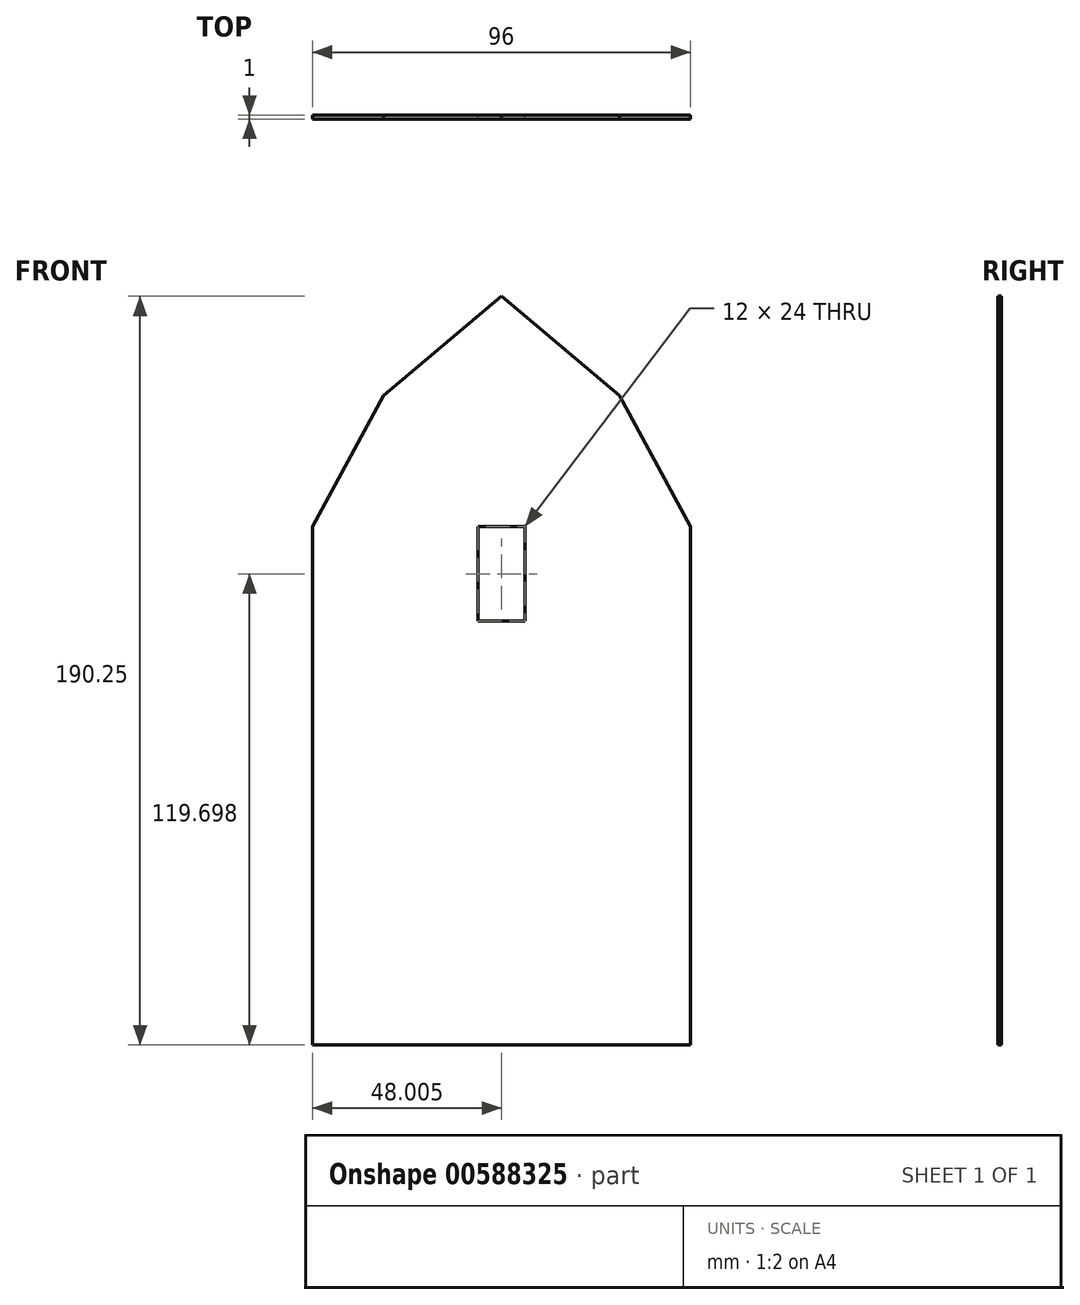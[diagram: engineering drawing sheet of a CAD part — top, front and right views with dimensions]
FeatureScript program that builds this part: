
annotation { "Feature Type Name" : "Feature", "Feature Type Description" : "" }
export const myFeature = defineFeature(function(context is Context, id is Id, definition is map)
    precondition{}
    {
        {
            var Q0;
            Q0=qCreatedBy(makeId("Front.planeOp"),FACE);
            var sketch = newSketch(context, id + "F0", { "sketchPlane" : qUnion([Q0])});
            skLineSegment(sketch, "E0", {"start": v(118.21, 7.75) * mm, "end": v(118.21, 40.5) * mm});
            skLineSegment(sketch, "E1", {"start": v(118.21, 40.5) * mm, "end": v(118.21, 113.5) * mm});
            skLineSegment(sketch, "E2", {"start": v(118.21, 113.5) * mm, "end": v(118.21, 116.7) * mm});
            skLineSegment(sketch, "E3", {"start": v(76.21, 116.7) * mm, "end": v(64.21, 116.7) * mm});
            skLineSegment(sketch, "E4", {"start": v(118.21, 7.75) * mm, "end": v(70.21, 7.75) * mm});
            skLineSegment(sketch, "E5", {"start": v(22.21, 7.75) * mm, "end": v(22.21, 116.7) * mm});
            skLineSegment(sketch, "E6", {"start": v(70.21, 116.7) * mm, "end": v(76.21, 116.7) * mm});
            skLineSegment(sketch, "E7", {"start": v(76.21, 116.7) * mm, "end": v(76.21, 92.7) * mm});
            skLineSegment(sketch, "E8", {"start": v(76.21, 92.7) * mm, "end": v(64.21, 92.7) * mm});
            skLineSegment(sketch, "E9", {"start": v(64.21, 92.7) * mm, "end": v(64.21, 116.7) * mm});
            skLineSegment(sketch, "E10", {"start": v(64.21, 116.7) * mm, "end": v(76.21, 116.7) * mm});
            skPoint(sketch, "E11.trimOffspring.end.orphan", {"position": v(70.21, 7.75) * mm});
            skLineSegment(sketch, "E12", {"start": v(100.21, 150) * mm, "end": v(118.21, 116.7) * mm});
            skLineSegment(sketch, "E13", {"start": v(70.21, 175.25) * mm, "end": v(100.21, 150) * mm});
            skLineSegment(sketch, "E14", {"start": v(75.71, 150) * mm, "end": v(64.71, 150) * mm});
            skLineSegment(sketch, "E15", {"start": v(70.21, 175.25) * mm, "end": v(40.21, 150) * mm});
            skLineSegment(sketch, "E16", {"start": v(22.21, 116.7) * mm, "end": v(40.21, 150) * mm});
            skLineSegment(sketch, "E17", {"start": v(70.21, 150) * mm, "end": v(64.71, 150) * mm});
            skLineSegment(sketch, "E18", {"start": v(64.71, 162) * mm, "end": v(75.71, 162) * mm});
            skLineSegment(sketch, "E19", {"start": v(75.71, 150) * mm, "end": v(70.21, 150) * mm});
            skLineSegment(sketch, "E20", {"start": v(70.21, 175.25) * mm, "end": v(70.21, 116.7) * mm});
            skLineSegment(sketch, "E21", {"start": v(22.21, 7.75) * mm, "end": v(22.21, -15) * mm});
            skLineSegment(sketch, "E22", {"start": v(22.21, -15) * mm, "end": v(118.21, -15) * mm});
            skLineSegment(sketch, "E23", {"start": v(118.21, -15) * mm, "end": v(118.21, 7.75) * mm});
            skSolve(sketch);
        }
        {
            var Q0;
            Q0=makeQuery(id+"F0.imprint","IMPRINT",FACE,{"disambiguationData":[TD([[makeQuery(id+"F0.imprint","IMPRINT",EDGE,{"derivedFrom":sQuery(id+"F0.wireOp",EDGE,"E0")}),1.0]])]});
            extrude(context, id + "F1", {"entities" : qUnion([Q0]), "depth" : 1 * mm, "offsetDistance" : 25 * mm});
        }
    });
